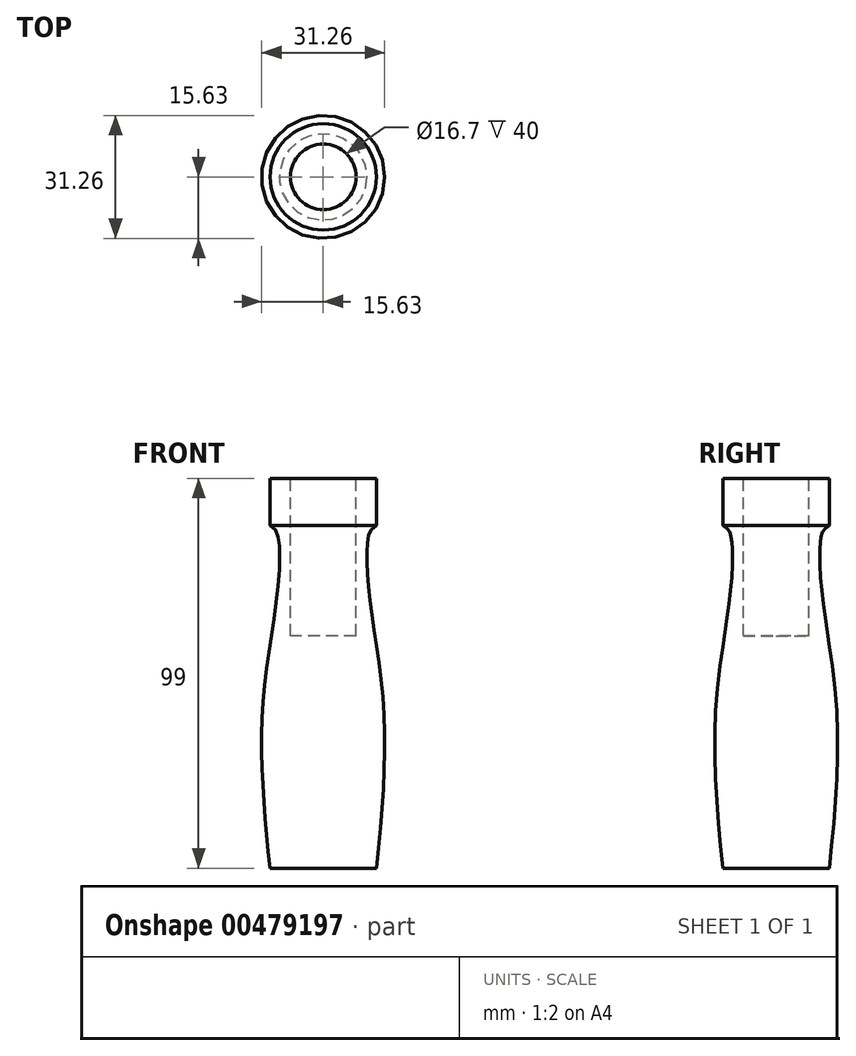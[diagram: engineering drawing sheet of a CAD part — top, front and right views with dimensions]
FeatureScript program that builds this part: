
annotation { "Feature Type Name" : "Feature", "Feature Type Description" : "" }
export const myFeature = defineFeature(function(context is Context, id is Id, definition is map)
    precondition{}
    {
        {
            var Q0;
            Q0=qCreatedBy(makeId("Front.planeOp"),FACE);
            var sketch = newSketch(context, id + "F0", { "sketchPlane" : qUnion([Q0])});
            skLineSegment(sketch, "E0", {"start": v(0, 0) * mm, "end": v(13.5, 0) * mm});
            skLineSegment(sketch, "E1", {"start": v(13.5, 0) * mm, "end": v(13.5, -12) * mm});
            skLineSegment(sketch, "E2", {"start": v(13.5, -99) * mm, "end": v(0, -99) * mm});
            skLineSegment(sketch, "E3", {"start": v(0, -99) * mm, "end": v(0, 0) * mm});
            skFitSpline(sketch, "E4", {"points": [v(13.5, -12) * mm, v(11.26, -15.9) * mm, v(11.69, -29.53) * mm, v(15.37, -58.54) * mm, v(13.5, -99) * mm], "startDerivative": vector(-41, -19.73) * mm, "endDerivative": vector(-12.95, -118.52) * mm});
            skLineSegment(sketch, "E5", {"start": v(0, 25.88) * mm, "end": v(0, 7.48) * mm, "construction": true});
            skSolve(sketch);
        }
        {
            var Q0;
            Q0=makeQuery(id+"F0.imprint","IMPRINT",FACE,{"disambiguationData":[TD([[makeQuery(id+"F0.imprint","IMPRINT",EDGE,{"derivedFrom":sQuery(id+"F0.wireOp",EDGE,"E0")}),-1.0]])]});
            var Q1;
            Q1=sQuery(id+"F0.wireOp",EDGE,"E5");
            revolve(context, id + "F1", {"entities" : qUnion([Q0]), "axis" : qUnion([Q1]), "revolveType" : RevolveType.FULL});
        }
        {
            var Q0;
            Q0=qCreatedBy(makeId("Top.planeOp"),FACE);
            var sketch = newSketch(context, id + "F2", { "sketchPlane" : qUnion([Q0])});
            skCircle(sketch, "E6", {"center": v(0, 0) * mm, "radius": 8.35 * mm});
            skSolve(sketch);
        }
        {
            var Q0;
            Q0 = qSketchRegion(id + "F2", true);
            extrude(context, id + "F3", {"entities" : qUnion([Q0]), "operationType" : NewBodyOperationType.REMOVE, "oppositeDirection" : true, "depth" : 40 * mm});
        }
    });
